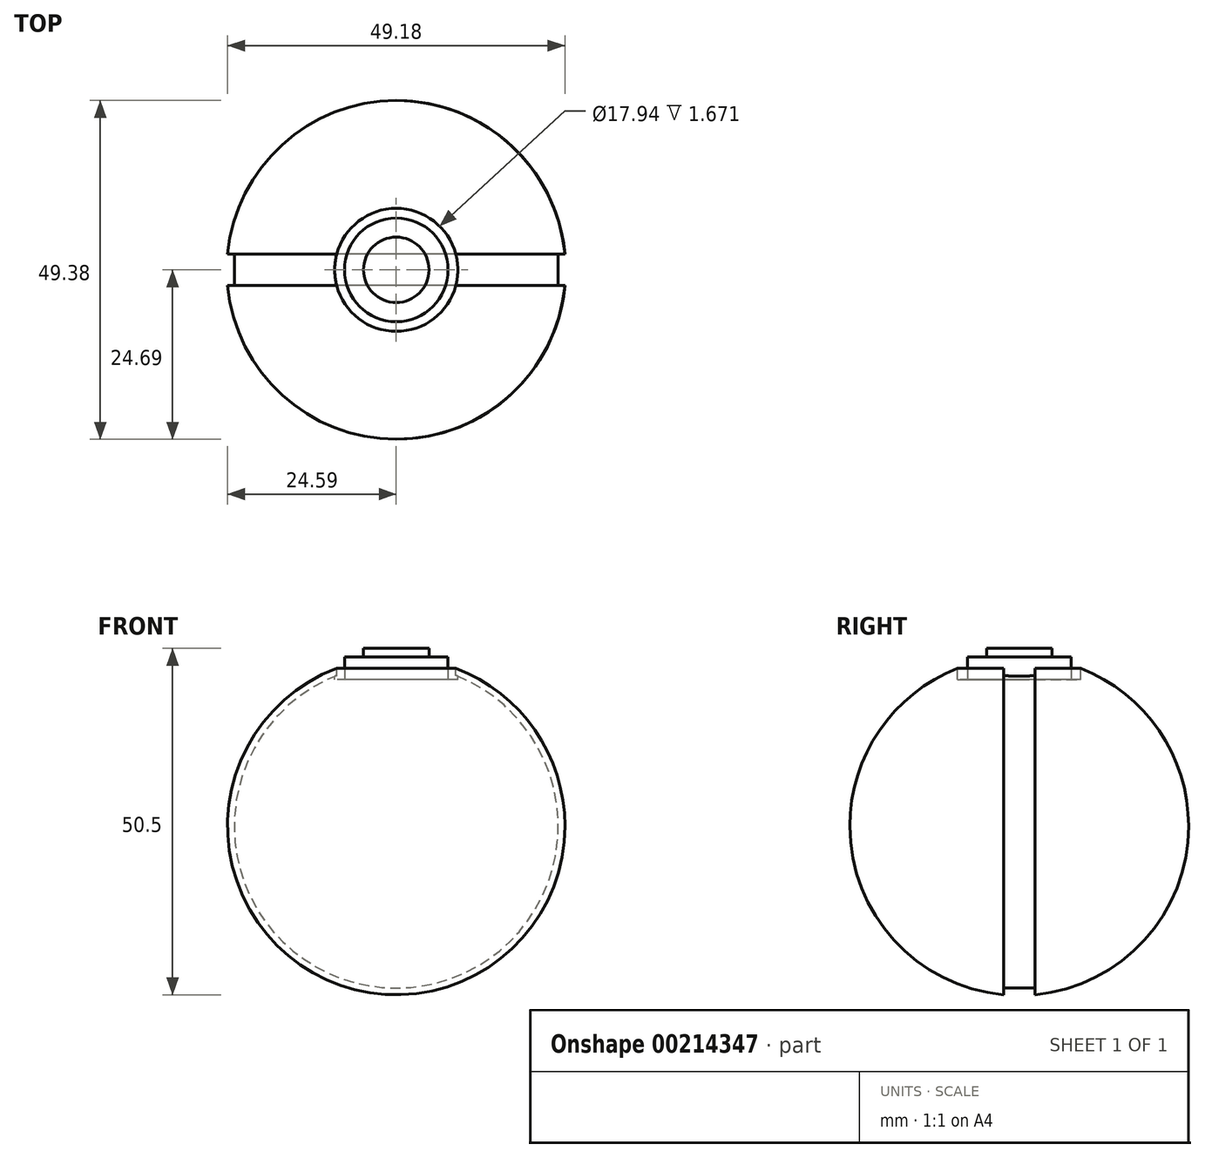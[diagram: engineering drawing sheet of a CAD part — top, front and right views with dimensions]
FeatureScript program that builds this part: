
annotation { "Feature Type Name" : "Feature", "Feature Type Description" : "" }
export const myFeature = defineFeature(function(context is Context, id is Id, definition is map)
    precondition{}
    {
        {
            var Q0;
            Q0=qCreatedBy(makeId("Top.planeOp"),FACE);
            var sketch = newSketch(context, id + "F0", { "sketchPlane" : qUnion([Q0])});
            skArc(sketch, "E0", {"start": v(0, -24.7) * mm, "mid": v(24.7, 0) * mm, "end": v(0, 24.7) * mm});
            skLineSegment(sketch, "E1", {"start": v(0, 24.7) * mm, "end": v(0, -24.7) * mm});
            skLineSegment(sketch, "E2", {"start": v(24.59, 2.3) * mm, "end": v(24.59, -2.3) * mm});
            skLineSegment(sketch, "E3", {"start": v(24.59, -2.3) * mm, "end": v(23.61, -2.3) * mm});
            skLineSegment(sketch, "E4", {"start": v(23.61, -2.3) * mm, "end": v(23.61, 2.3) * mm});
            skLineSegment(sketch, "E5", {"start": v(23.61, 2.3) * mm, "end": v(24.59, 2.3) * mm});
            skSolve(sketch);
        }
        {
            var Q0;
            Q0=qCreatedBy(makeId("Top.planeOp"),FACE);
            var sketch = newSketch(context, id + "F1", { "sketchPlane" : qUnion([Q0])});
            skLineSegment(sketch, "E6", {"start": v(0, 25.13) * mm, "end": v(0, -24.47) * mm});
            skLineSegment(sketch, "E7", {"start": v(0, -24.47) * mm, "end": v(0, 25.13) * mm, "construction": true});
            skSolve(sketch);
        }
        {
            var Q0;
            {var subQ0=sQuery(id+"F0.wireOp",EDGE,"E1");Q0=makeQuery(id+"F0.imprint","IMPRINT",FACE,{"disambiguationData":[TD([[makeQuery(id+"F0.imprint","IMPRINT",EDGE,{"derivedFrom":subQ0}),1.0]])]});}
            var Q1;
            {var subQ0=sQuery(id+"F0.wireOp",EDGE,"BjEeamoj-oghQ-JpOv-Se7c-AkbNBiQ3d7iG");Q1=makeQuery(id+"F0.imprint","IMPRINT",FACE,{"disambiguationData":[TD([[makeQuery(id+"F0.imprint","IMPRINT",EDGE,{"derivedFrom":subQ0}),1.0]])]});}
            var Q2;
            {var subQ0=sQuery(id+"F0.wireOp",EDGE,"ZKSApend-aVRa-FWlX-GppA-htd5diSxhR72");Q2=makeQuery(id+"F0.imprint","IMPRINT",FACE,{"disambiguationData":[TD([[makeQuery(id+"F0.imprint","IMPRINT",EDGE,{"derivedFrom":subQ0}),-1.0]])]});}
            var Q3;
            Q3=sQuery(id+"F1.wireOp",EDGE,"E6");
            revolve(context, id + "F2", {"entities" : qUnion([Q0, Q1, Q2]), "axis" : qUnion([Q3]), "revolveType" : RevolveType.FULL});
        }
        {
            var Q0;
            Q0=qCreatedBy(makeId("Top.planeOp"),FACE);
            var sketch = newSketch(context, id + "F3", { "sketchPlane" : qUnion([Q0])});
            skCircle(sketch, "E8", {"center": v(0, 0) * mm, "radius": 4.77 * mm});
            skSolve(sketch);
        }
        {
            var Q0;
            Q0 = qSketchRegion(id + "F3", true);
            extrude(context, id + "F4", {"entities" : qUnion([Q0]), "operationType" : NewBodyOperationType.ADD, "depth" : 25.9 * mm});
        }
        {
            var Q0;
            Q0=qCreatedBy(makeId("Top.planeOp"),FACE);
            var sketch = newSketch(context, id + "F5", { "sketchPlane" : qUnion([Q0])});
            skCircle(sketch, "E9", {"center": v(0, 0) * mm, "radius": 7.56 * mm});
            skSolve(sketch);
        }
        {
            var Q0;
            Q0 = qSketchRegion(id + "F5", true);
            extrude(context, id + "F6", {"entities" : qUnion([Q0]), "operationType" : NewBodyOperationType.ADD, "depth" : 24.64 * mm});
        }
        {
            var Q0;
            Q0=makeQuery(id+"F6.opExtrude","CAP_FACE",FACE,{"disambiguationData":[OSD([sQuery(id+"F5.wireOp",EDGE,"E9")])],"isStart":false});
            var sketch = newSketch(context, id + "F7", { "sketchPlane" : qUnion([Q0])});
            skCircle(sketch, "E10", {"center": v(0, 0) * mm, "radius": 8.97 * mm});
            skCircle(sketch, "E11.0", {"center": v(0, 0) * mm, "radius": 7.56 * mm});
            skSolve(sketch);
        }
        {
            var Q0;
            Q0 = qSketchRegion(id + "F7", true);
            extrude(context, id + "F8", {"entities" : qUnion([Q0]), "operationType" : NewBodyOperationType.REMOVE, "oppositeDirection" : true, "depth" : 3.3 * mm});
        }
    });
